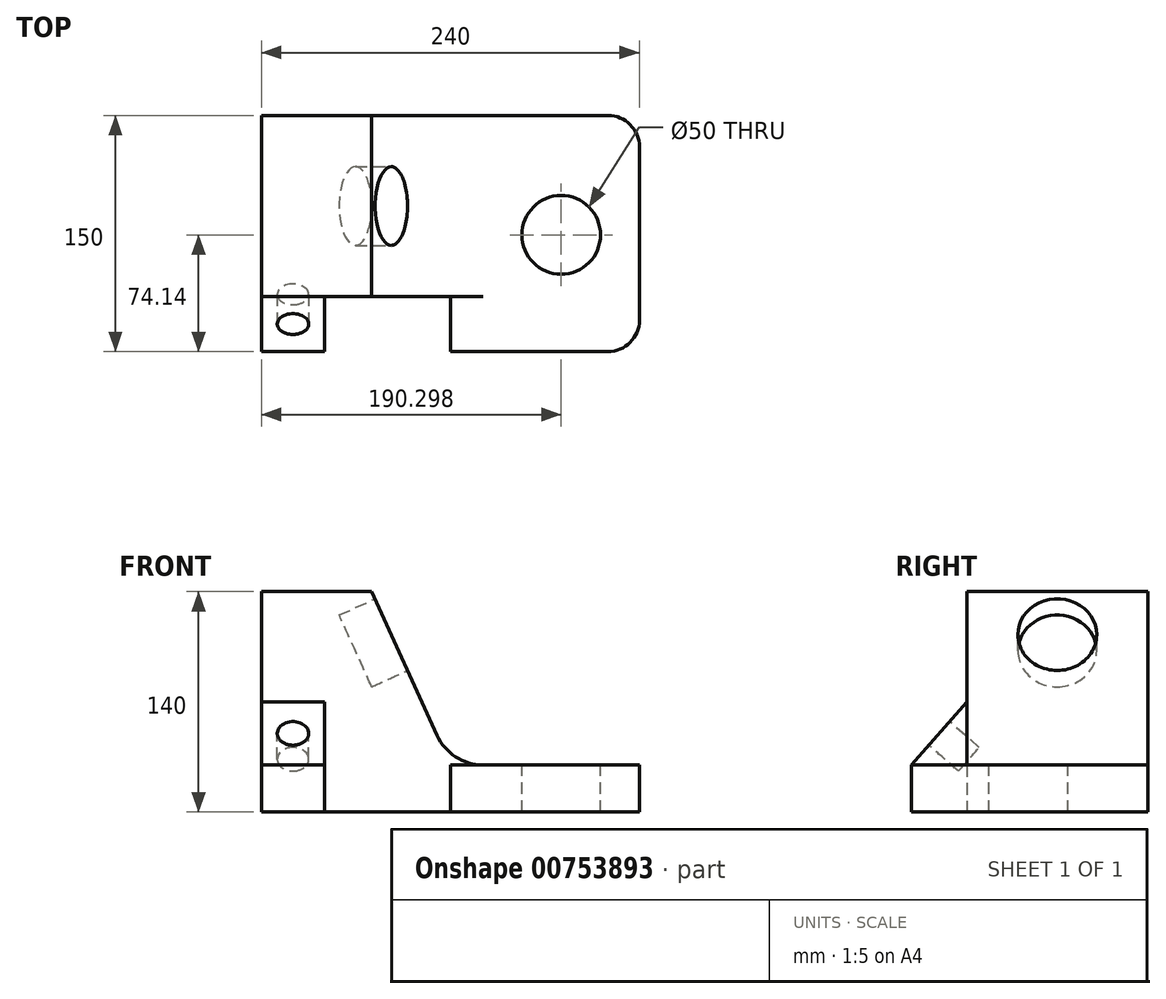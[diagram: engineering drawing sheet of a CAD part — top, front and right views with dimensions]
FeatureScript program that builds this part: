
annotation { "Feature Type Name" : "Feature", "Feature Type Description" : "" }
export const myFeature = defineFeature(function(context is Context, id is Id, definition is map)
    precondition{}
    {
        {
            var Q0;
            Q0=qCreatedBy(makeId("Top.planeOp"),FACE);
            var sketch = newSketch(context, id + "F0", { "sketchPlane" : qUnion([Q0])});
            skLineSegment(sketch, "E0", {"start": v(-63.92, 106.48) * mm, "end": v(-63.92, -43.52) * mm});
            skLineSegment(sketch, "E1", {"start": v(-63.92, -43.52) * mm, "end": v(-23.92, -43.52) * mm});
            skLineSegment(sketch, "E2", {"start": v(-23.92, -43.52) * mm, "end": v(-23.92, -8.52) * mm});
            skLineSegment(sketch, "E3", {"start": v(-23.92, -8.52) * mm, "end": v(-63.92, -8.52) * mm});
            skLineSegment(sketch, "E4", {"start": v(-63.92, 106.48) * mm, "end": v(176.08, 106.48) * mm});
            skLineSegment(sketch, "E5", {"start": v(176.08, 106.48) * mm, "end": v(176.08, -43.52) * mm});
            skLineSegment(sketch, "E6", {"start": v(176.08, -43.52) * mm, "end": v(56.08, -43.52) * mm});
            skLineSegment(sketch, "E7", {"start": v(56.08, -43.52) * mm, "end": v(56.08, -8.52) * mm});
            skLineSegment(sketch, "E8", {"start": v(56.08, -8.52) * mm, "end": v(-23.92, -8.52) * mm});
            skLineSegment(sketch, "E9", {"start": v(56.08, -8.52) * mm, "end": v(56.08, 106.48) * mm});
            skSolve(sketch);
        }
        {
            var Q0;
            Q0 = qSketchRegion(id + "F0", true);
            extrude(context, id + "F1", {"entities" : qUnion([Q0]), "depth" : 30 * mm, "offsetDistance" : 25 * mm});
        }
        {
            var Q0;
            {var subQ0=sQuery(id+"F0.wireOp",EDGE,"E1");Q0=makeQuery(id+"F0.imprint","IMPRINT",FACE,{"disambiguationData":[TD([[makeQuery(id+"F0.imprint","IMPRINT",EDGE,{"derivedFrom":subQ0}),1.0]])]});}
            extrude(context, id + "F2", {"entities" : qUnion([Q0]), "depth" : 70 * mm, "offsetDistance" : 25 * mm});
        }
        {
            var Q0;
            Q0=makeQuery(id+"F2.opExtrude","SWEPT_FACE",FACE,{"disambiguationData":[OSD([sQuery(id+"F0.wireOp",EDGE,"E2")])]});
            var sketch = newSketch(context, id + "F3", { "sketchPlane" : qUnion([Q0])});
            skLineSegment(sketch, "E10.0.0", {"start": v(-43.52, 0) * mm, "end": v(-8.52, 0) * mm});
            skLineSegment(sketch, "E10.0.1", {"start": v(-8.52, 0) * mm, "end": v(-8.52, 30) * mm});
            skLineSegment(sketch, "E10.0.2", {"start": v(-8.52, 30) * mm, "end": v(-43.52, 30) * mm});
            skLineSegment(sketch, "E10.0.3", {"start": v(-43.52, 30) * mm, "end": v(-43.52, 0) * mm});
            skLineSegment(sketch, "E11.0.1", {"start": v(-43.52, 0) * mm, "end": v(-43.52, 70) * mm});
            skLineSegment(sketch, "E11.0.3", {"start": v(-43.52, 70) * mm, "end": v(-43.52, 0) * mm});
            skLineSegment(sketch, "E12.0.1", {"start": v(-43.52, 0) * mm, "end": v(-43.52, 30) * mm});
            skLineSegment(sketch, "E13.0.1", {"start": v(-8.52, 0) * mm, "end": v(-8.52, 70) * mm});
            skLineSegment(sketch, "E13.0.2", {"start": v(-8.52, 70) * mm, "end": v(-43.52, 70) * mm});
            skLineSegment(sketch, "E14", {"start": v(-8.52, 70) * mm, "end": v(-43.52, 30) * mm});
            skSolve(sketch);
        }
        {
            var Q0;
            {var subQ0=sQuery(id+"F3.wireOp",EDGE,"E13.0.2");Q0=makeQuery(id+"F3.imprint","IMPRINT",FACE,{"disambiguationData":[TD([[makeQuery(id+"F3.imprint","IMPRINT",EDGE,{"derivedFrom":subQ0}),-1.0]])]});}
            extrude(context, id + "F4", {"entities" : qUnion([Q0]), "operationType" : NewBodyOperationType.REMOVE, "oppositeDirection" : true, "depth" : 96 * mm, "offsetDistance" : 25 * mm});
        }
        {
            var Q0;
            {var subQ0=sQuery(id+"F0.wireOp",EDGE,"E3");Q0=makeQuery(id+"F0.imprint","IMPRINT",FACE,{"disambiguationData":[TD([[makeQuery(id+"F0.imprint","IMPRINT",EDGE,{"derivedFrom":subQ0}),-1.0]])]});}
            extrude(context, id + "F5", {"entities" : qUnion([Q0]), "operationType" : NewBodyOperationType.ADD, "depth" : 140 * mm, "offsetDistance" : 25 * mm});
        }
        {
            var Q0;
            Q0=makeQuery(id+"F4.boolean.opBoolean","COPY",FACE,{"derivedFrom":makeQuery(id+"F4.opExtrude","SWEPT_FACE",FACE,{"disambiguationData":[OSD([sQuery(id+"F3.wireOp",EDGE,"E14")])]})});
            var sketch = newSketch(context, id + "F6", { "sketchPlane" : qUnion([Q0])});
            skLineSegment(sketch, "E15", {"start": v(-43.92, 47.07) * mm, "end": v(-43.92, -6.08) * mm});
            skCircle(sketch, "E16", {"center": v(-43.92, 20.5) * mm, "radius": 10 * mm});
            skSolve(sketch);
        }
        {
            var Q0;
            {var subQ0=sQuery(id+"F0.wireOp",EDGE,"E8");Q0=makeQuery(id+"F5.boolean.opBoolean","MERGE",FACE,{"derivedFrom":[makeQuery(id+"F1.opExtrude","SWEPT_FACE",FACE,{"disambiguationData":[OSD([subQ0])]}),makeQuery(id+"F5.opExtrude","SWEPT_FACE",FACE,{"disambiguationData":[OSD([sQuery(id+"F0.wireOp",EDGE,"E3"),subQ0])]})]});}
            var sketch = newSketch(context, id + "F7", { "sketchPlane" : qUnion([Q0])});
            skLineSegment(sketch, "E17.0.0", {"start": v(-23.92, 0) * mm, "end": v(56.08, 0) * mm});
            skLineSegment(sketch, "E17.0.1", {"start": v(56.08, 0) * mm, "end": v(56.08, 30) * mm});
            skLineSegment(sketch, "E17.0.2", {"start": v(56.08, 30) * mm, "end": v(56.08, 140) * mm});
            skLineSegment(sketch, "E17.0.3", {"start": v(56.08, 140) * mm, "end": v(-63.92, 140) * mm});
            skLineSegment(sketch, "E17.0.4", {"start": v(-63.92, 140) * mm, "end": v(-63.92, 70) * mm});
            skLineSegment(sketch, "E17.0.5", {"start": v(-63.92, 70) * mm, "end": v(-23.92, 70) * mm});
            skLineSegment(sketch, "E17.0.6", {"start": v(-23.92, 70) * mm, "end": v(-23.92, 0) * mm});
            skLineSegment(sketch, "E18", {"start": v(-63.92, 140) * mm, "end": v(6.08, 140) * mm});
            skLineSegment(sketch, "E19", {"start": v(6.08, 140) * mm, "end": v(56.08, 30) * mm});
            skSolve(sketch);
        }
        {
            var Q0;
            Q0=makeQuery(id+"F7.imprint","IMPRINT",FACE,{"disambiguationData":[TD([[makeQuery(id+"F7.imprint","IMPRINT",EDGE,{"derivedFrom":sQuery(id+"F7.wireOp",EDGE,"E17.0.2")}),-1.0]])]});
            extrude(context, id + "F8", {"entities" : qUnion([Q0]), "operationType" : NewBodyOperationType.REMOVE, "oppositeDirection" : true, "depth" : 248 * mm, "offsetDistance" : 25 * mm});
        }
        {
            var Q0;
            {var subQ0=sQuery(id+"F6.wireOp",EDGE,"E16");var subQ1=sQuery(id+"F6.wireOp",EDGE,"E15");var subQ2=makeQuery(id+"F6.imprint","INTERSECT",VERTEX,{"disambiguationData":[OD(0.0)],"derivedFrom":[subQ1,subQ0]});Q0=makeQuery(id+"F6.imprint","IMPRINT",FACE,{"disambiguationData":[TD([[makeQuery(id+"F6.imprint","IMPRINT",EDGE,{"disambiguationData":[TD([[subQ2,-1.0]])],"derivedFrom":subQ1}),1.0]])]});}
            var Q1;
            {var subQ0=sQuery(id+"F6.wireOp",EDGE,"E16");var subQ1=sQuery(id+"F6.wireOp",EDGE,"E15");var subQ2=makeQuery(id+"F6.imprint","INTERSECT",VERTEX,{"disambiguationData":[OD(0.0)],"derivedFrom":[subQ1,subQ0]});Q1=makeQuery(id+"F6.imprint","IMPRINT",FACE,{"disambiguationData":[TD([[makeQuery(id+"F6.imprint","IMPRINT",EDGE,{"disambiguationData":[TD([[subQ2,-1.0]])],"derivedFrom":subQ1}),-1.0]])]});}
            extrude(context, id + "F9", {"entities" : qUnion([Q0, Q1]), "operationType" : NewBodyOperationType.REMOVE, "oppositeDirection" : true, "depth" : 25 * mm, "offsetDistance" : 25 * mm});
        }
        {
            var Q0;
            Q0=makeQuery(id+"F8.boolean.opBoolean","MERGE",EDGE,{"derivedFrom":[makeQuery(id+"F5.boolean.opBoolean","INTERSECT",EDGE,{"derivedFrom":[makeQuery(id+"F1.opExtrude","CAP_FACE",FACE,{"disambiguationData":[OSD([sQuery(id+"F0.wireOp",EDGE,"E0"),sQuery(id+"F0.wireOp",EDGE,"E1"),sQuery(id+"F0.wireOp",EDGE,"E2"),sQuery(id+"F0.wireOp",EDGE,"E4"),sQuery(id+"F0.wireOp",EDGE,"E5"),sQuery(id+"F0.wireOp",EDGE,"E6"),sQuery(id+"F0.wireOp",EDGE,"E7"),sQuery(id+"F0.wireOp",EDGE,"E8")])],"isStart":false}),makeQuery(id+"F5.opExtrude","SWEPT_FACE",FACE,{"disambiguationData":[OSD([sQuery(id+"F0.wireOp",EDGE,"E9")])]})]}),makeQuery(id+"F8.opExtrude","SWEPT_EDGE",EDGE,{"disambiguationData":[OSD([sQuery(id+"F7.wireOp",EDGE,"E17.0.1"),sQuery(id+"F7.wireOp",EDGE,"E17.0.2"),sQuery(id+"F7.wireOp",EDGE,"E19")])]})]});
            fillet(context, id + "F10", {"entities" : qUnion([Q0]), "radius" : 32 * mm, "tangentPropagation" : true, "allowEdgeOverflow" : false});
        }
        {
            var Q0;
            Q0=makeQuery(id+"F1.opExtrude","SWEPT_EDGE",EDGE,{"disambiguationData":[OSD([sQuery(id+"F0.wireOp",EDGE,"E4"),sQuery(id+"F0.wireOp",EDGE,"E5")])]});
            var Q1;
            Q1=makeQuery(id+"F1.opExtrude","SWEPT_EDGE",EDGE,{"disambiguationData":[OSD([sQuery(id+"F0.wireOp",EDGE,"E5"),sQuery(id+"F0.wireOp",EDGE,"E6")])]});
            fillet(context, id + "F11", {"entities" : qUnion([Q0, Q1]), "radius" : 20 * mm, "tangentPropagation" : true, "allowEdgeOverflow" : false});
        }
        {
            var Q0;
            Q0=makeQuery(id+"F1.opExtrude","CAP_FACE",FACE,{"disambiguationData":[OSD([sQuery(id+"F0.wireOp",EDGE,"E0"),sQuery(id+"F0.wireOp",EDGE,"E1"),sQuery(id+"F0.wireOp",EDGE,"E2"),sQuery(id+"F0.wireOp",EDGE,"E4"),sQuery(id+"F0.wireOp",EDGE,"E5"),sQuery(id+"F0.wireOp",EDGE,"E6"),sQuery(id+"F0.wireOp",EDGE,"E7"),sQuery(id+"F0.wireOp",EDGE,"E8")])],"isStart":false});
            var sketch = newSketch(context, id + "F12", { "sketchPlane" : qUnion([Q0])});
            skLineSegment(sketch, "E20", {"start": v(176.08, 31.48) * mm, "end": v(76.68, 29.76) * mm});
            skCircle(sketch, "E21", {"center": v(126.38, 30.62) * mm, "radius": 25 * mm});
            skSolve(sketch);
        }
        {
            var Q0;
            Q0 = qSketchRegion(id + "F12", true);
            extrude(context, id + "F13", {"entities" : qUnion([Q0]), "operationType" : NewBodyOperationType.REMOVE, "oppositeDirection" : true, "depth" : 140 * mm, "offsetDistance" : 25 * mm});
        }
        {
            var Q0;
            Q0=makeQuery(id+"F8.boolean.opBoolean","COPY",FACE,{"derivedFrom":makeQuery(id+"F8.opExtrude","SWEPT_FACE",FACE,{"disambiguationData":[OSD([sQuery(id+"F7.wireOp",EDGE,"E19")])]})});
            var sketch = newSketch(context, id + "F14", { "sketchPlane" : qUnion([Q0])});
            skLineSegment(sketch, "E22", {"start": v(48.98, 124.94) * mm, "end": v(48.98, 24.71) * mm});
            skLineSegment(sketch, "E23", {"start": v(48.98, 124.94) * mm, "end": v(48.98, 107.17) * mm});
            skLineSegment(sketch, "E24", {"start": v(48.98, 124.94) * mm, "end": v(48.98, 94.94) * mm});
            skCircle(sketch, "E25", {"center": v(48.98, 94.94) * mm, "radius": 25 * mm});
            skSolve(sketch);
        }
        {
            var Q0;
            Q0 = qSketchRegion(id + "F14", true);
            extrude(context, id + "F15", {"entities" : qUnion([Q0]), "operationType" : NewBodyOperationType.REMOVE, "oppositeDirection" : true, "depth" : 25 * mm, "offsetDistance" : 25 * mm});
        }
    });
